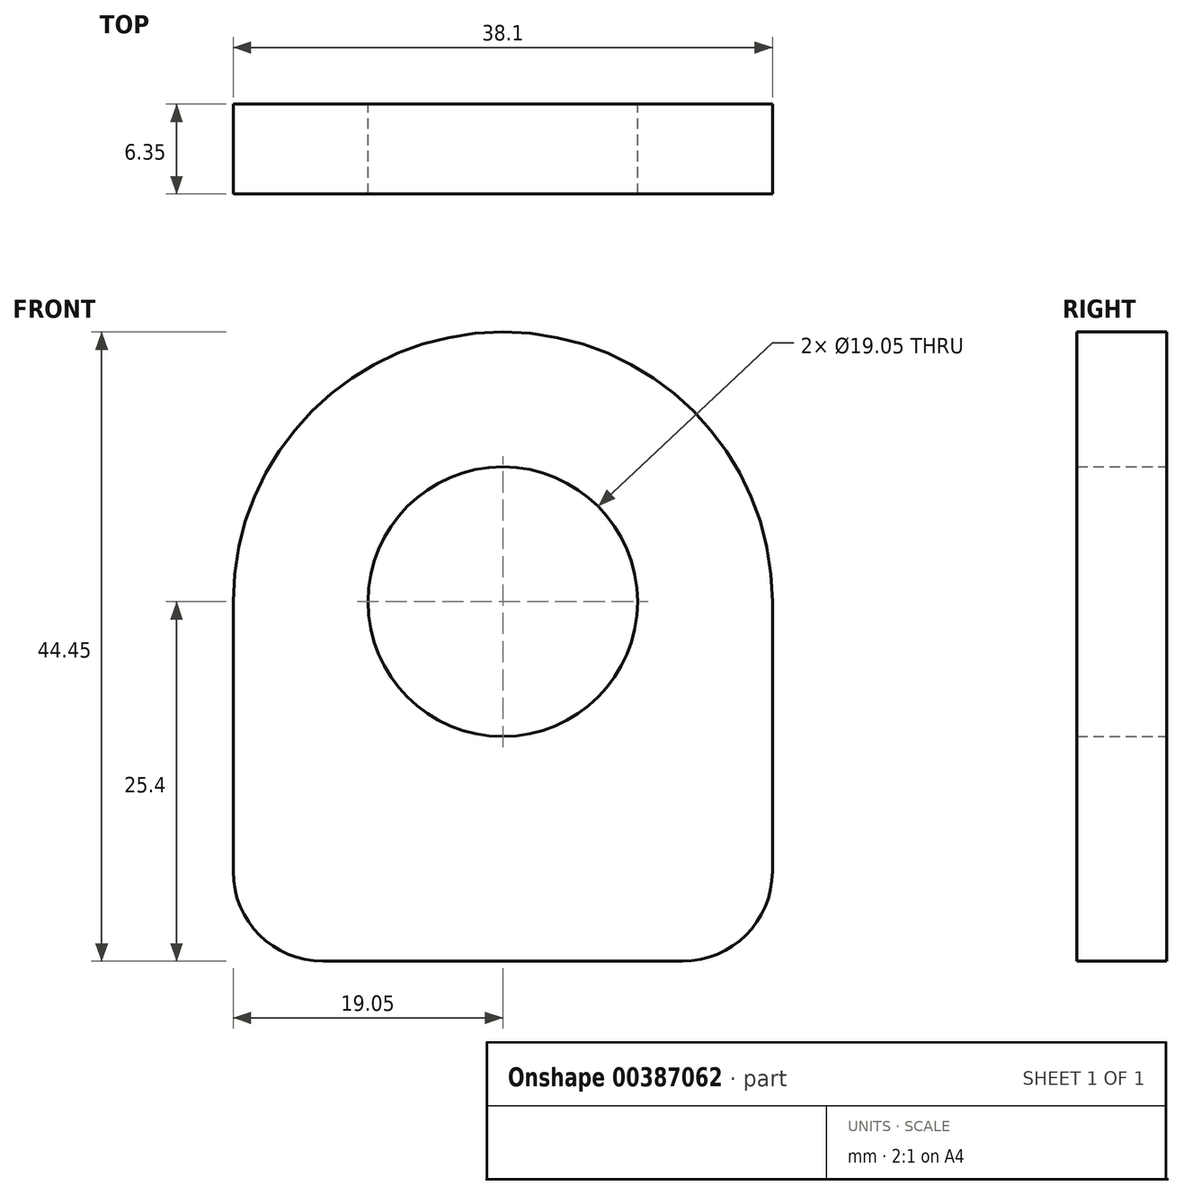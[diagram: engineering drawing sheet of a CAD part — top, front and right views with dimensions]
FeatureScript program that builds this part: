
annotation { "Feature Type Name" : "Feature", "Feature Type Description" : "" }
export const myFeature = defineFeature(function(context is Context, id is Id, definition is map)
    precondition{}
    {
        {
            var Q0;
            Q0=qCreatedBy(makeId("Front.planeOp"),FACE);
            var sketch = newSketch(context, id + "F0", { "sketchPlane" : qUnion([Q0])});
            skLineSegment(sketch, "E0", {"start": v(6.35, 0) * mm, "end": v(31.75, 0) * mm});
            skLineSegment(sketch, "E1", {"start": v(38.1, 6.35) * mm, "end": v(38.1, 25.4) * mm});
            skLineSegment(sketch, "E2", {"start": v(38.1, 25.4) * mm, "end": v(0, 25.4) * mm});
            skLineSegment(sketch, "E3", {"start": v(0, 25.4) * mm, "end": v(0, 6.35) * mm});
            skArc(sketch, "E4", {"start": v(38.1, 25.4) * mm, "mid": v(19.05, 44.45) * mm, "end": v(0, 25.4) * mm});
            skCircle(sketch, "E5", {"center": v(19.05, 25.4) * mm, "radius": 9.53 * mm});
            skPoint(sketch, "E6.visualSharp", {"position": v(0, 0) * mm});
            skArc(sketch, "E6.filletArc", {"start": v(0, 6.35) * mm, "mid": v(1.86, 1.86) * mm, "end": v(6.35, 0) * mm});
            skPoint(sketch, "E7.visualSharp", {"position": v(38.1, 0) * mm});
            skArc(sketch, "E7.filletArc", {"start": v(31.75, 0) * mm, "mid": v(36.24, 1.86) * mm, "end": v(38.1, 6.35) * mm});
            skSolve(sketch);
        }
        {
            var Q0;
            {var subQ0=sQuery(id+"F0.wireOp",EDGE,"E4");Q0=makeQuery(id+"F0.imprint","IMPRINT",FACE,{"disambiguationData":[TD([[makeQuery(id+"F0.imprint","IMPRINT",EDGE,{"derivedFrom":subQ0}),1.0]])]});}
            var Q1;
            Q1=makeQuery(id+"F0.imprint","IMPRINT",FACE,{"disambiguationData":[TD([[makeQuery(id+"F0.imprint","IMPRINT",EDGE,{"derivedFrom":sQuery(id+"F0.wireOp",EDGE,"E0")}),1.0]])]});
            extrude(context, id + "F1", {"entities" : qUnion([Q0, Q1]), "depth" : 6.35 * mm});
        }
    });
